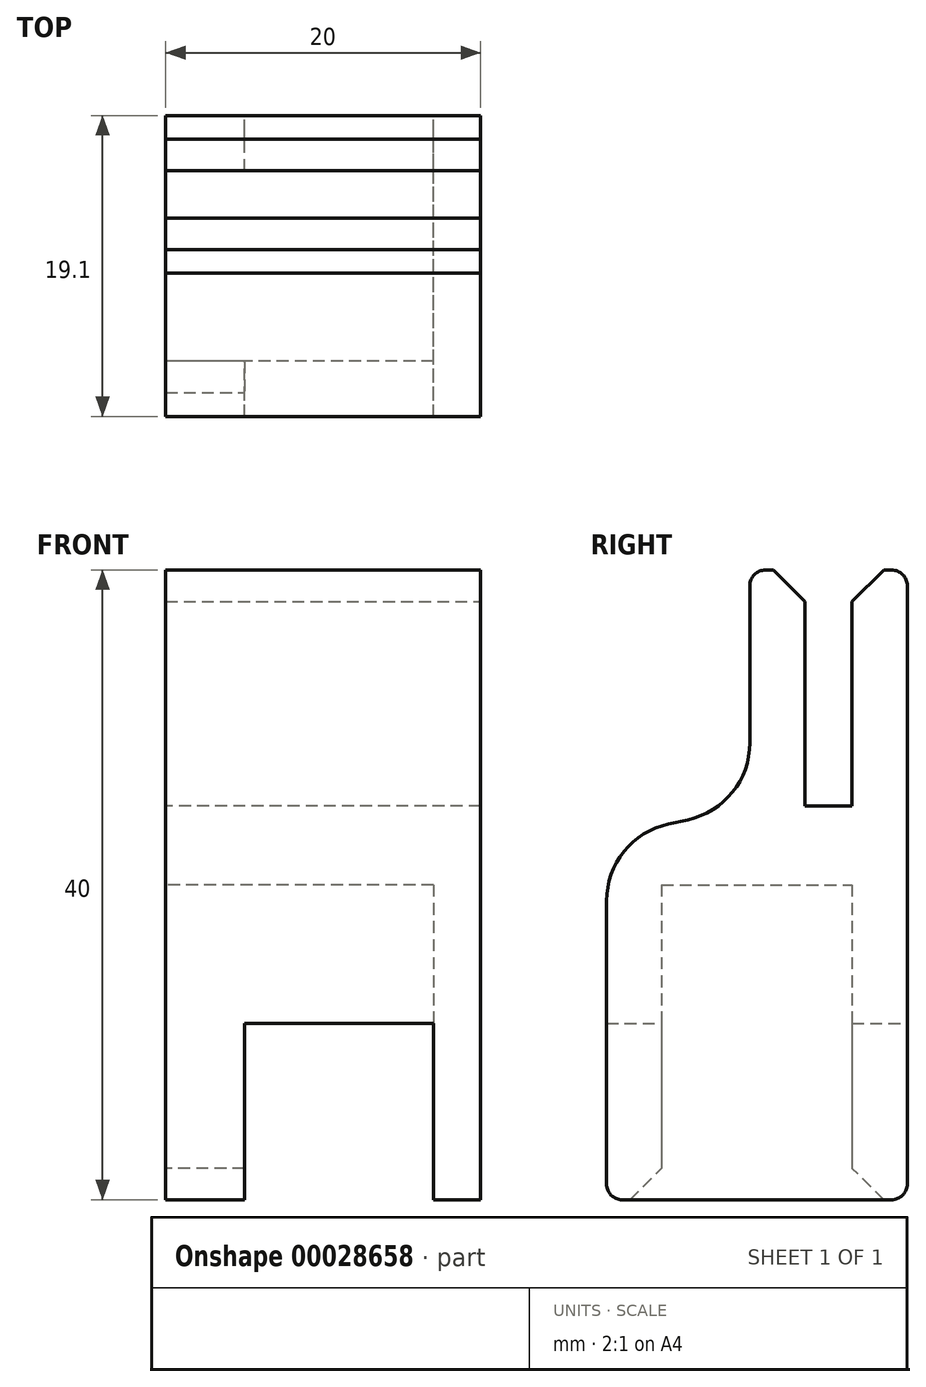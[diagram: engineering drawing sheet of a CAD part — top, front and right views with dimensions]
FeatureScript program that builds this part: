
annotation { "Feature Type Name" : "Feature", "Feature Type Description" : "" }
export const myFeature = defineFeature(function(context is Context, id is Id, definition is map)
    precondition{}
    {
        {
            var Q0;
            Q0=qCreatedBy(makeId("Right.planeOp"),FACE);
            var sketch = newSketch(context, id + "F0", { "sketchPlane" : qUnion([Q0])});
            skLineSegment(sketch, "E0.top", {"start": v(-3, 2.6) * mm, "end": v(0, 2.6) * mm});
            skLineSegment(sketch, "E0.left", {"start": v(-3, 17.6) * mm, "end": v(-3, 2.6) * mm});
            skLineSegment(sketch, "E0.right", {"start": v(0, 17.6) * mm, "end": v(0, 2.6) * mm});
            skLineSegment(sketch, "E1.bottom", {"start": v(-12.1, -2.4) * mm, "end": v(0, -2.4) * mm});
            skLineSegment(sketch, "E1.left", {"start": v(-12.1, -2.4) * mm, "end": v(-12.1, -22.4) * mm});
            skLineSegment(sketch, "E1.right", {"start": v(0, -2.4) * mm, "end": v(0, -22.4) * mm});
            skLineSegment(sketch, "E2", {"start": v(0, 17.6) * mm, "end": v(3.5, 17.6) * mm});
            skLineSegment(sketch, "E3", {"start": v(3.5, 17.6) * mm, "end": v(3.5, -22.4) * mm});
            skLineSegment(sketch, "E4", {"start": v(3.5, -22.4) * mm, "end": v(0, -22.4) * mm});
            skLineSegment(sketch, "E5", {"start": v(-15.6, -22.4) * mm, "end": v(-15.6, 0.6) * mm});
            skLineSegment(sketch, "E6", {"start": v(-15.6, 0.6) * mm, "end": v(-6.5, 2.6) * mm});
            skLineSegment(sketch, "E7", {"start": v(-6.5, 2.6) * mm, "end": v(-6.5, 17.6) * mm});
            skLineSegment(sketch, "E8", {"start": v(-6.5, 17.6) * mm, "end": v(-3, 17.6) * mm});
            skLineSegment(sketch, "E9.trimOffspring", {"start": v(-12.1, -22.4) * mm, "end": v(-15.6, -22.4) * mm});
            skSolve(sketch);
        }
        {
            var Q0;
            Q0 = qSketchRegion(id + "F0", true);
            extrude(context, id + "F1", {"entities" : qUnion([Q0]), "depth" : 20 * mm});
        }
        {
            var Q0;
            Q0=makeQuery(id+"F1.opExtrude","CAP_FACE",FACE,{"disambiguationData":[OSD([sQuery(id+"F0.wireOp",EDGE,"E0.top"),sQuery(id+"F0.wireOp",EDGE,"E0.left"),sQuery(id+"F0.wireOp",EDGE,"E0.right"),sQuery(id+"F0.wireOp",EDGE,"E1.bottom"),sQuery(id+"F0.wireOp",EDGE,"E1.left"),sQuery(id+"F0.wireOp",EDGE,"E1.right"),sQuery(id+"F0.wireOp",EDGE,"E3"),sQuery(id+"F0.wireOp",EDGE,"E4"),sQuery(id+"F0.wireOp",EDGE,"E5"),sQuery(id+"F0.wireOp",EDGE,"E6"),sQuery(id+"F0.wireOp",EDGE,"E7"),sQuery(id+"F0.wireOp",EDGE,"E8"),sQuery(id+"F0.wireOp",EDGE,"E2"),sQuery(id+"F0.wireOp",EDGE,"E9.trimOffspring")])],"isStart":false});
            var sketch = newSketch(context, id + "F2", { "sketchPlane" : qUnion([Q0])});
            skLineSegment(sketch, "E10.bottom", {"start": v(-14.5, -22.4) * mm, "end": v(2.15, -22.4) * mm});
            skLineSegment(sketch, "E10.top", {"start": v(-14.5, -0.08) * mm, "end": v(2.15, -0.08) * mm});
            skLineSegment(sketch, "E10.left", {"start": v(-14.5, -22.4) * mm, "end": v(-14.5, -0.08) * mm});
            skLineSegment(sketch, "E10.right", {"start": v(2.15, -22.4) * mm, "end": v(2.15, -0.08) * mm});
            skSolve(sketch);
        }
        {
            var Q0;
            Q0 = qSketchRegion(id + "F2", true);
            extrude(context, id + "F3", {"entities" : qUnion([Q0]), "operationType" : NewBodyOperationType.ADD, "oppositeDirection" : true, "depth" : 3 * mm});
        }
        {
            var Q0;
            Q0=makeQuery(id+"F1.opExtrude","SWEPT_EDGE",EDGE,{"disambiguationData":[OSD([sQuery(id+"F0.wireOp",EDGE,"E6"),sQuery(id+"F0.wireOp",EDGE,"E7")])]});
            var Q1;
            Q1=makeQuery(id+"F1.opExtrude","SWEPT_EDGE",EDGE,{"disambiguationData":[OSD([sQuery(id+"F0.wireOp",EDGE,"E5"),sQuery(id+"F0.wireOp",EDGE,"E6")])]});
            fillet(context, id + "F4", {"entities" : qUnion([Q0, Q1]), "radius" : 5 * mm, "tangentPropagation" : true, "allowEdgeOverflow" : false});
        }
        {
            var Q0;
            Q0=makeQuery(id+"F1.opExtrude","SWEPT_FACE",FACE,{"disambiguationData":[OSD([sQuery(id+"F0.wireOp",EDGE,"E3")])]});
            var sketch = newSketch(context, id + "F5", { "sketchPlane" : qUnion([Q0])});
            skLineSegment(sketch, "E11.bottom", {"start": v(-17, -11.2) * mm, "end": v(-5, -11.2) * mm});
            skLineSegment(sketch, "E11.top", {"start": v(-17, -22.4) * mm, "end": v(-5, -22.4) * mm});
            skLineSegment(sketch, "E11.left", {"start": v(-17, -11.2) * mm, "end": v(-17, -22.4) * mm});
            skLineSegment(sketch, "E11.right", {"start": v(-5, -11.2) * mm, "end": v(-5, -22.4) * mm});
            skSolve(sketch);
        }
        {
            var Q0;
            Q0 = qSketchRegion(id + "F5", true);
            var Q1;
            Q1=makeQuery(id+"F1.opExtrude","SWEPT_FACE",FACE,{"disambiguationData":[OSD([sQuery(id+"F0.wireOp",EDGE,"E5")])]});
            extrude(context, id + "F6", {"entities" : qUnion([Q0]), "operationType" : NewBodyOperationType.REMOVE, "endBound" : BoundingType.UP_TO_SURFACE, "oppositeDirection" : true, "endBoundEntityFace" : qUnion([Q1]), "depth" : 25 * mm});
        }
        {
            var Q0;
            Q0=makeQuery(id+"F1.opExtrude","SWEPT_EDGE",EDGE,{"disambiguationData":[OSD([sQuery(id+"F0.wireOp",EDGE,"E1.right"),sQuery(id+"F0.wireOp",EDGE,"E4")])]});
            var Q1;
            Q1=makeQuery(id+"F1.opExtrude","SWEPT_EDGE",EDGE,{"disambiguationData":[OSD([sQuery(id+"F0.wireOp",EDGE,"E1.left"),sQuery(id+"F0.wireOp",EDGE,"E9.trimOffspring")])]});
            var Q2;
            Q2=makeQuery(id+"F1.opExtrude","SWEPT_EDGE",EDGE,{"disambiguationData":[OSD([sQuery(id+"F0.wireOp",EDGE,"E0.right"),sQuery(id+"F0.wireOp",EDGE,"E2")])]});
            var Q3;
            Q3=makeQuery(id+"F1.opExtrude","SWEPT_EDGE",EDGE,{"disambiguationData":[OSD([sQuery(id+"F0.wireOp",EDGE,"E0.left"),sQuery(id+"F0.wireOp",EDGE,"E8")])]});
            chamfer(context, id + "F7", {"entities" : qUnion([Q0, Q1, Q2, Q3]), "width" : 2 * mm, "tangentPropagation" : true});
        }
        {
            var Q0;
            Q0=makeQuery(id+"F1.opExtrude","SWEPT_EDGE",EDGE,{"disambiguationData":[OSD([sQuery(id+"F0.wireOp",EDGE,"E3"),sQuery(id+"F0.wireOp",EDGE,"E2")])]});
            var Q1;
            Q1=makeQuery(id+"F1.opExtrude","SWEPT_EDGE",EDGE,{"disambiguationData":[OSD([sQuery(id+"F0.wireOp",EDGE,"E7"),sQuery(id+"F0.wireOp",EDGE,"E8")])]});
            var Q2;
            {var subQ0=sQuery(id+"F0.wireOp",EDGE,"E9.trimOffspring");var subQ1=sQuery(id+"F0.wireOp",EDGE,"E5");Q2=makeQuery(id+"F6.boolean.opBoolean","SPLIT",EDGE,{"disambiguationData":[TD([makeQuery(id+"F6.opExtrude","SWEPT_FACE",FACE,{"disambiguationData":[OSD([sQuery(id+"F5.wireOp",EDGE,"E11.left")])]})])],"derivedFrom":makeQuery(id+"F1.opExtrude","SWEPT_EDGE",EDGE,{"disambiguationData":[OSD([subQ1,subQ0])]})});}
            var Q3;
            {var subQ0=sQuery(id+"F0.wireOp",EDGE,"E9.trimOffspring");var subQ1=sQuery(id+"F0.wireOp",EDGE,"E5");Q3=makeQuery(id+"F6.boolean.opBoolean","SPLIT",EDGE,{"disambiguationData":[TD([makeQuery(id+"F6.opExtrude","SWEPT_FACE",FACE,{"disambiguationData":[OSD([sQuery(id+"F5.wireOp",EDGE,"E11.right")])]})])],"derivedFrom":makeQuery(id+"F1.opExtrude","SWEPT_EDGE",EDGE,{"disambiguationData":[OSD([subQ1,subQ0])]})});}
            var Q4;
            {var subQ1=sQuery(id+"F0.wireOp",EDGE,"E4");var subQ2=sQuery(id+"F0.wireOp",EDGE,"E3");Q4=makeQuery(id+"F6.boolean.opBoolean","SPLIT",EDGE,{"disambiguationData":[TD([makeQuery(id+"F6.opExtrude","SWEPT_FACE",FACE,{"disambiguationData":[OSD([sQuery(id+"F5.wireOp",EDGE,"E11.left")])]})])],"derivedFrom":makeQuery(id+"F1.opExtrude","SWEPT_EDGE",EDGE,{"disambiguationData":[OSD([subQ2,subQ1])]})});}
            var Q5;
            {var subQ1=sQuery(id+"F0.wireOp",EDGE,"E4");var subQ2=sQuery(id+"F0.wireOp",EDGE,"E3");Q5=makeQuery(id+"F6.boolean.opBoolean","SPLIT",EDGE,{"disambiguationData":[TD([makeQuery(id+"F6.opExtrude","SWEPT_FACE",FACE,{"disambiguationData":[OSD([sQuery(id+"F5.wireOp",EDGE,"E11.right")])]})])],"derivedFrom":makeQuery(id+"F1.opExtrude","SWEPT_EDGE",EDGE,{"disambiguationData":[OSD([subQ2,subQ1])]})});}
            fillet(context, id + "F8", {"entities" : qUnion([Q0, Q1, Q2, Q3, Q4, Q5]), "radius" : 1 * mm, "tangentPropagation" : true, "allowEdgeOverflow" : false});
        }
    });
